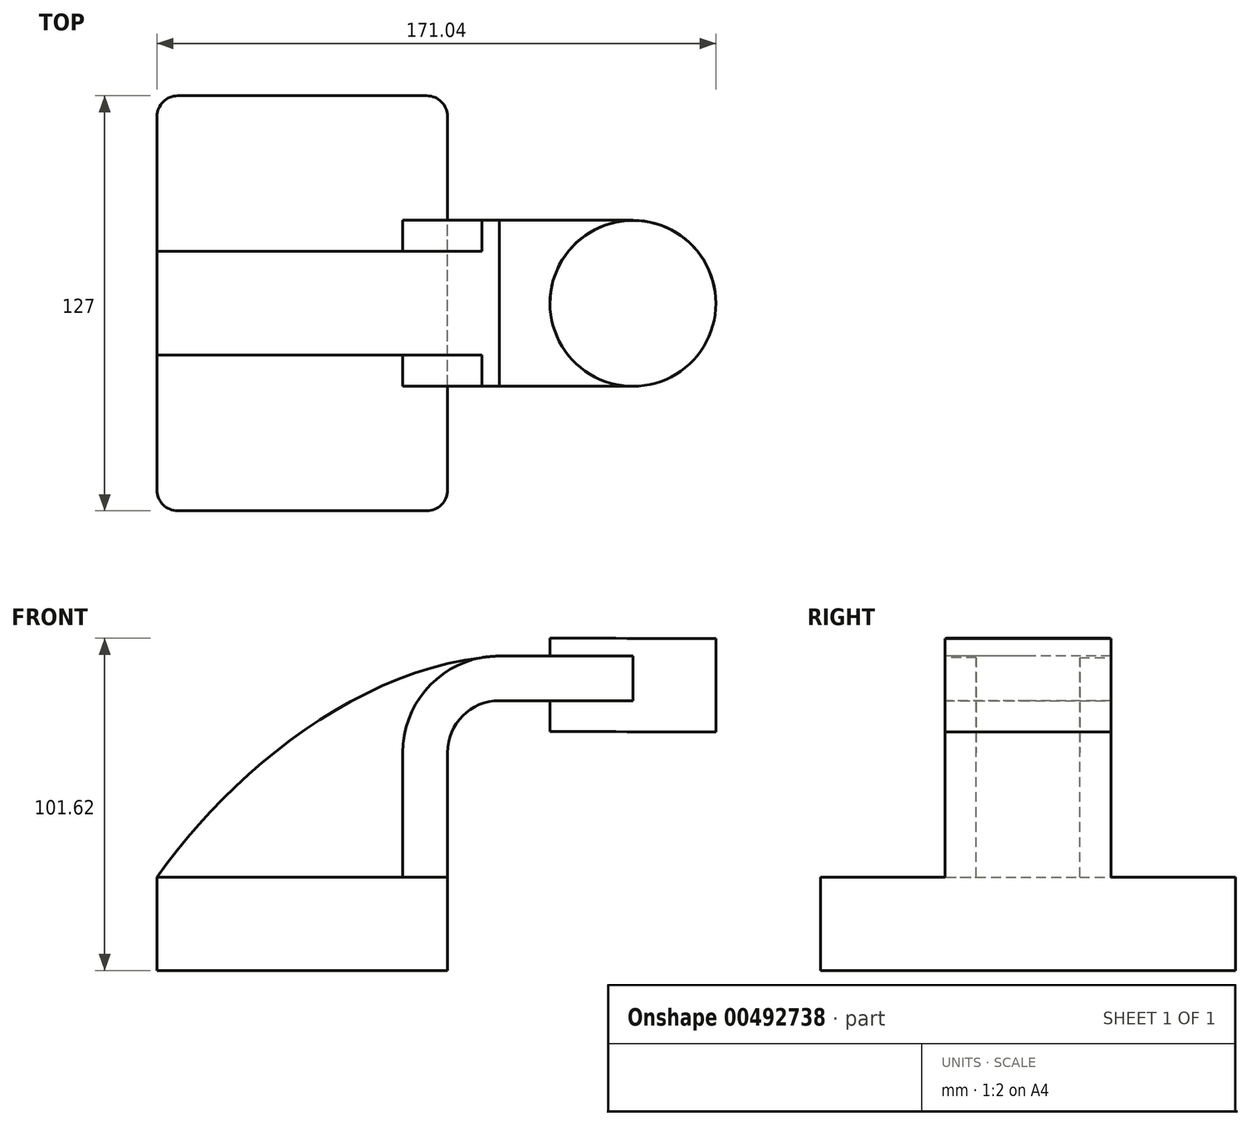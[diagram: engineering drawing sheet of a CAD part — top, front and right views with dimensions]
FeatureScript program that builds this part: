
annotation { "Feature Type Name" : "Feature", "Feature Type Description" : "" }
export const myFeature = defineFeature(function(context is Context, id is Id, definition is map)
    precondition{}
    {
        {
            var Q0;
            Q0=qCreatedBy(makeId("Front.planeOp"),FACE);
            var sketch = newSketch(context, id + "F0", { "sketchPlane" : qUnion([Q0])});
            skLineSegment(sketch, "E0.bottom", {"start": v(-44.45, 14.29) * mm, "end": v(44.45, 14.29) * mm});
            skLineSegment(sketch, "E0.top", {"start": v(-44.45, -14.29) * mm, "end": v(44.45, -14.29) * mm});
            skLineSegment(sketch, "E0.left", {"start": v(-44.45, 14.29) * mm, "end": v(-44.45, -14.29) * mm});
            skLineSegment(sketch, "E0.right", {"start": v(44.45, 14.29) * mm, "end": v(44.45, -14.29) * mm});
            skPoint(sketch, "E0.middle", {"position": v(0, 0) * mm});
            skLineSegment(sketch, "E1.bottom", {"start": v(75.79, 58.74) * mm, "end": v(126.59, 58.74) * mm});
            skLineSegment(sketch, "E1.top", {"start": v(75.79, 87.31) * mm, "end": v(126.59, 87.31) * mm});
            skLineSegment(sketch, "E1.left", {"start": v(75.79, 58.74) * mm, "end": v(75.79, 87.31) * mm});
            skLineSegment(sketch, "E1.right", {"start": v(126.59, 58.74) * mm, "end": v(126.59, 87.31) * mm});
            skPoint(sketch, "E1.middle", {"position": v(101.19, 73.03) * mm});
            skLineSegment(sketch, "E2", {"start": v(44.45, 14.29) * mm, "end": v(44.45, 52.39) * mm});
            skArc(sketch, "E3", {"start": v(44.45, 52.39) * mm, "mid": v(49.1, 63.61) * mm, "end": v(60.32, 68.26) * mm});
            skLineSegment(sketch, "E4", {"start": v(60.32, 68.26) * mm, "end": v(101.2, 68.26) * mm});
            skLineSegment(sketch, "E5.0", {"start": v(60.32, 81.95) * mm, "end": v(101.2, 81.95) * mm});
            skArc(sketch, "E5.1", {"start": v(30.76, 52.39) * mm, "mid": v(39.42, 73.3) * mm, "end": v(60.32, 81.95) * mm});
            skLineSegment(sketch, "E5.2", {"start": v(30.76, 14.29) * mm, "end": v(30.76, 52.39) * mm});
            skLineSegment(sketch, "E6", {"start": v(101.19, 58.74) * mm, "end": v(101.2, 87.31) * mm});
            skFitSpline(sketch, "E7", {"points": [v(-44.45, 14.29) * mm, v(60.32, 81.95) * mm], "startDerivative": vector(69.15, 97.57) * mm, "endDerivative": vector(126.14, 7.78) * mm});
            skSolve(sketch);
        }
        {
            var Q0;
            Q0=makeQuery(id+"F0.imprint","IMPRINT",FACE,{"disambiguationData":[TD([[makeQuery(id+"F0.imprint","IMPRINT",EDGE,{"derivedFrom":sQuery(id+"F0.wireOp",EDGE,"E0.top")}),1.0]])]});
            extrude(context, id + "F1", {"entities" : qUnion([Q0]), "endBound" : BoundingType.SYMMETRIC, "depth" : 127 * mm});
        }
        {
            var Q0;
            {var subQ1=sQuery(id+"F0.wireOp",EDGE,"E2");Q0=makeQuery(id+"F0.imprint","IMPRINT",FACE,{"disambiguationData":[TD([[makeQuery(id+"F0.imprint","IMPRINT",EDGE,{"derivedFrom":subQ1}),1.0]])]});}
            var Q1;
            {var subQ0=sQuery(id+"F0.wireOp",EDGE,"E4");var subQ1=sQuery(id+"F0.wireOp",EDGE,"E1.left");var subQ2=makeQuery(id+"F0.imprint","INTERSECT",VERTEX,{"derivedFrom":[subQ1,subQ0]});Q1=makeQuery(id+"F0.imprint","IMPRINT",FACE,{"disambiguationData":[TD([[makeQuery(id+"F0.imprint","IMPRINT",EDGE,{"disambiguationData":[TD([[subQ2,-1.0]])],"derivedFrom":subQ1}),-1.0]])]});}
            extrude(context, id + "F2", {"entities" : qUnion([Q0, Q1]), "operationType" : NewBodyOperationType.ADD, "endBound" : BoundingType.SYMMETRIC, "depth" : 50.8 * mm});
        }
        {
            var Q0;
            {var subQ3=sQuery(id+"F0.wireOp",EDGE,"E5.2");Q0=makeQuery(id+"F0.imprint","IMPRINT",FACE,{"disambiguationData":[TD([[makeQuery(id+"F0.imprint","IMPRINT",EDGE,{"derivedFrom":subQ3}),1.0]])]});}
            extrude(context, id + "F3", {"entities" : qUnion([Q0]), "operationType" : NewBodyOperationType.ADD, "endBound" : BoundingType.SYMMETRIC, "depth" : 31.75 * mm});
        }
        {
            var Q0;
            {var subQ4=sQuery(id+"F0.wireOp",EDGE,"E1.right");Q0=makeQuery(id+"F0.imprint","IMPRINT",FACE,{"disambiguationData":[TD([[makeQuery(id+"F0.imprint","IMPRINT",EDGE,{"derivedFrom":subQ4}),1.0]])]});}
            var Q1;
            Q1=sQuery(id+"F0.wireOp",EDGE,"E6");
            revolve(context, id + "F4", {"operationType" : NewBodyOperationType.ADD, "entities" : qUnion([Q0]), "axis" : qUnion([Q1]), "revolveType" : RevolveType.FULL});
        }
        {
            var Q0;
            Q0=makeQuery(id+"F1.opExtrude","CAP_EDGE",EDGE,{"disambiguationData":[OSD([sQuery(id+"F0.wireOp",EDGE,"E0.left")])],"isStart":true});
            var Q1;
            Q1=makeQuery(id+"F1.opExtrude","CAP_EDGE",EDGE,{"disambiguationData":[OSD([sQuery(id+"F0.wireOp",EDGE,"E0.left")])],"isStart":false});
            var Q2;
            Q2=makeQuery(id+"F1.opExtrude","CAP_EDGE",EDGE,{"disambiguationData":[OSD([sQuery(id+"F0.wireOp",EDGE,"E0.right")])],"isStart":true});
            var Q3;
            Q3=makeQuery(id+"F1.opExtrude","CAP_EDGE",EDGE,{"disambiguationData":[OSD([sQuery(id+"F0.wireOp",EDGE,"E0.right")])],"isStart":false});
            fillet(context, id + "F5", {"entities" : qUnion([Q0, Q1, Q2, Q3]), "radius" : 6.35 * mm, "tangentPropagation" : true, "allowEdgeOverflow" : false});
        }
    });
